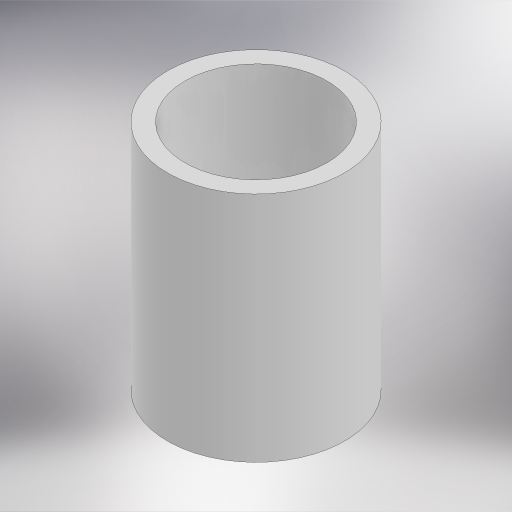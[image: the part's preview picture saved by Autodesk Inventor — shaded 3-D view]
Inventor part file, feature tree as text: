
AUTODESK INVENTOR PART (.ipt)
format: ipt  version: 2023 (Build 270158000, 158)  size: 252,416 bytes
history: native  units: in
note: dims shown in document units (in); Inventor stores cm internally (conversion verified against a paired STEP export)
features: other x1, extrude x1, sketch x1
ambient origin geometry x8: Origin, YZ Plane, XZ Plane, XY Plane, X Axis, Y Axis, Z Axis, Center Point
bodies: Body1 (feature_tree)
feature tree (3):
  other  "Sólido1"
  extrude  "Extrusión1"  Depth=1.378in
  sketch  "Boceto2"  dims[d1=1.0492in d2=0.8425in d3=1.378in d4=0.0in]
